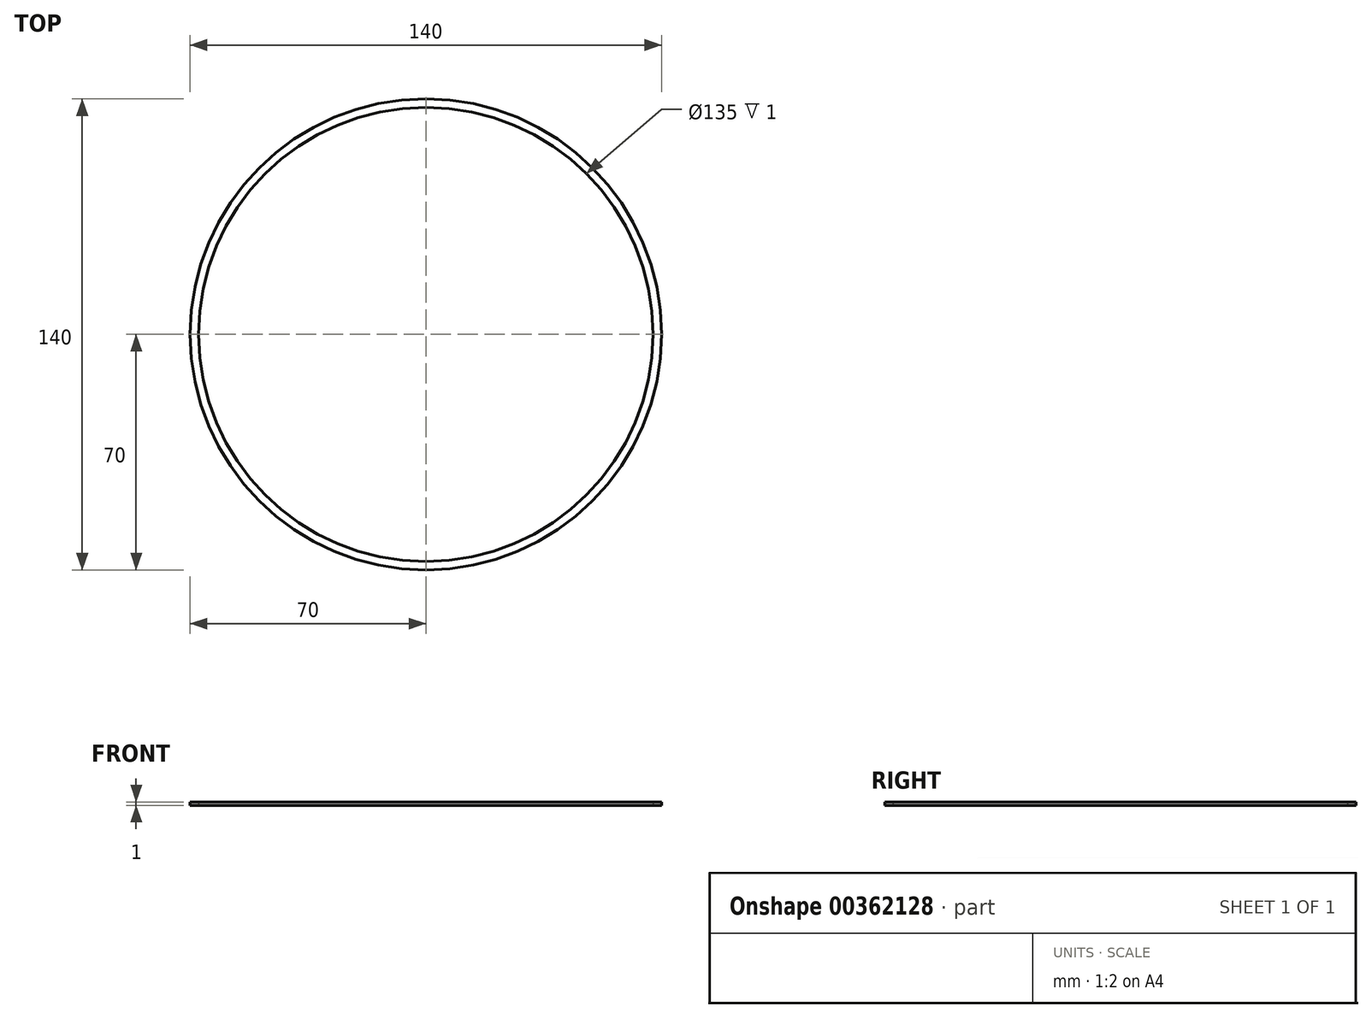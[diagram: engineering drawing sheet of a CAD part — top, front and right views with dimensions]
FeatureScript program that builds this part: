
annotation { "Feature Type Name" : "Feature", "Feature Type Description" : "" }
export const myFeature = defineFeature(function(context is Context, id is Id, definition is map)
    precondition{}
    {
        {
            var Q0;
            Q0=qCreatedBy(makeId("Top.planeOp"),FACE);
            var sketch = newSketch(context, id + "F0", { "sketchPlane" : qUnion([Q0])});
            skCircle(sketch, "E0", {"center": v(0, 0) * mm, "radius": 70 * mm});
            skCircle(sketch, "E1", {"center": v(0, 0) * mm, "radius": 67.5 * mm});
            skSolve(sketch);
        }
        {
            var Q0;
            Q0=makeQuery(id+"F0.imprint","IMPRINT",FACE,{"disambiguationData":[TD([[makeQuery(id+"F0.imprint","IMPRINT",EDGE,{"derivedFrom":sQuery(id+"F0.wireOp",EDGE,"E0")}),1.0]])]});
            extrude(context, id + "F1", {"entities" : qUnion([Q0]), "depth" : 1 * mm, "offsetDistance" : 25 * mm});
        }
    });
